# Revit family: TYCO-FPP-FireClass-FC410DIM DETECTOR IP MODULE
name_source: partatom
category: Electrical Fixtures
revit_build: Autodesk Revit 2014 (Build: 20130308_1515(x64)
units: mm (PartAtom-declared; Revit-internal decimal feet)

## types (1)
- TYCO-FPP-FireClass-FC410DIM DETECTOR IP MODULE
    Description = Conventional Zone
Monitor
    EOL Resistor Value = 4.7k Ohms
    Front Cover = Yes
    Keynote = The Addressable FC410DIM provides the ability to connect and Interface
one zone of conventional detectors (non-addressable) to the Fire Alarm Controller.
    Length = 61 mm
    Loop Voltage = 20V to 40Vdc
    Manufacturer = Tyco
    Model = FireClass - 555.800.712
    Operating Temperature = - 25 - + 70 ºC
    PCB = PCB
    Rear Cover = Yes
    Relative Humidity = 10% to 95%
    Storage Temperature = –40°C to +80°C
    Type Comments = The FC410DIM monitors the status of detectors and wiring to detectors and
signals detector and wiring status back to the Controller.
    URL = https://fireclass.co.uk
    Width = 84 mm
    Wire Size (maximum) = 2.5sq. mm

## geometry (parser evidence)
native form markers: Sweep x4
no freeform markers — native parametric forms only
